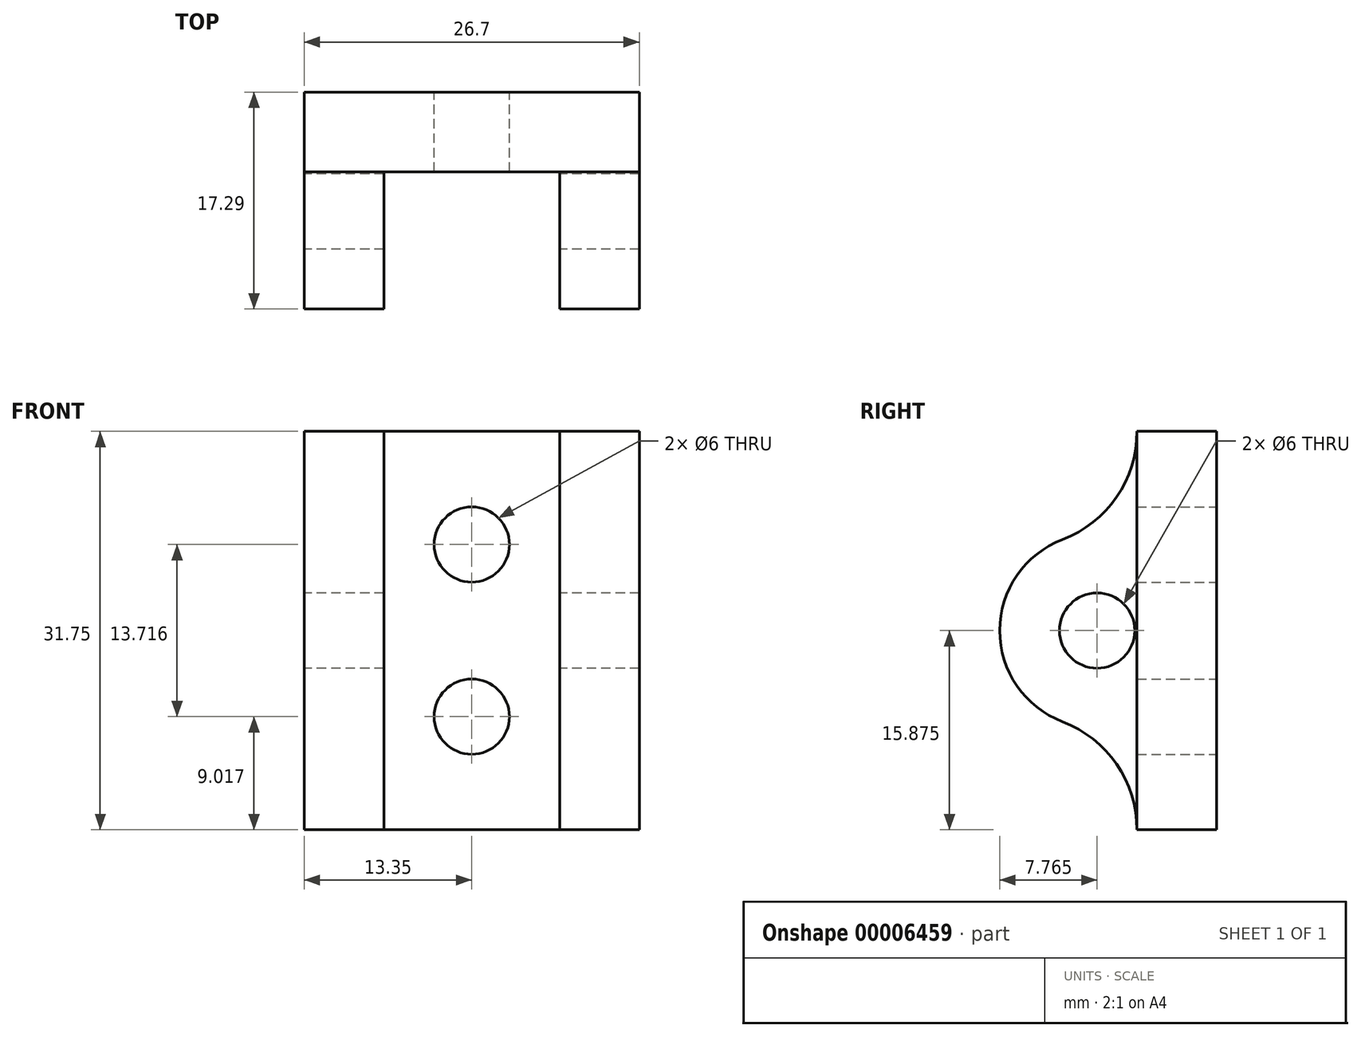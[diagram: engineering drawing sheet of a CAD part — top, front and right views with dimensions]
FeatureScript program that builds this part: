
annotation { "Feature Type Name" : "Feature", "Feature Type Description" : "" }
export const myFeature = defineFeature(function(context is Context, id is Id, definition is map)
    precondition{}
    {
        {
            var Q0;
            Q0=qCreatedBy(makeId("Front.planeOp"),FACE);
            var sketch = newSketch(context, id + "F0", { "sketchPlane" : qUnion([Q0])});
            skLineSegment(sketch, "E0.bottom", {"start": v(0, 0) * mm, "end": v(26.7, 0) * mm});
            skLineSegment(sketch, "E0.top", {"start": v(0, -31.75) * mm, "end": v(26.7, -31.75) * mm});
            skLineSegment(sketch, "E0.left", {"start": v(0, 0) * mm, "end": v(0, -31.75) * mm});
            skLineSegment(sketch, "E0.right", {"start": v(26.7, 0) * mm, "end": v(26.7, -31.75) * mm});
            skCircle(sketch, "E1", {"center": v(13.35, -22.73) * mm, "radius": 3 * mm});
            skCircle(sketch, "E2", {"center": v(13.35, -9.02) * mm, "radius": 3 * mm});
            skLineSegment(sketch, "E3", {"start": v(13.35, -9.02) * mm, "end": v(13.35, -22.73) * mm, "construction": true});
            skPoint(sketch, "E4", {"position": v(13.35, -31.75) * mm});
            skPoint(sketch, "E5", {"position": v(0, -15.88) * mm});
            skPoint(sketch, "E6", {"position": v(13.35, -15.88) * mm});
            skSolve(sketch);
        }
        {
            var Q0;
            Q0 = qSketchRegion(id + "F0", true);
            extrude(context, id + "F1", {"entities" : qUnion([Q0]), "depth" : 6.35 * mm});
        }
        {
            var Q0;
            Q0=makeQuery(id+"F1.opExtrude","SWEPT_FACE",FACE,{"disambiguationData":[OSD([sQuery(id+"F0.wireOp",EDGE,"E0.left")])]});
            var sketch = newSketch(context, id + "F2", { "sketchPlane" : qUnion([Q0])});
            skCircle(sketch, "E7", {"center": v(9.53, -15.88) * mm, "radius": 3 * mm});
            skPoint(sketch, "E8", {"position": v(6.35, -15.88) * mm});
            skArc(sketch, "E9", {"start": v(12.3, -23.13) * mm, "mid": v(17.29, -15.88) * mm, "end": v(12.3, -8.62) * mm});
            skArc(sketch, "E10", {"start": v(12.3, -23.13) * mm, "mid": v(7.98, -26.52) * mm, "end": v(6.35, -31.75) * mm});
            skArc(sketch, "E11", {"start": v(6.35, 0) * mm, "mid": v(7.98, -5.23) * mm, "end": v(12.3, -8.62) * mm});
            skLineSegment(sketch, "E12", {"start": v(6.35, 0) * mm, "end": v(6.35, -31.75) * mm});
            skSolve(sketch);
        }
        {
            var Q0;
            Q0=makeQuery(id+"F2.imprint","IMPRINT",FACE,{"disambiguationData":[TD([[makeQuery(id+"F2.imprint","IMPRINT",EDGE,{"derivedFrom":sQuery(id+"F2.wireOp",EDGE,"E7")}),-1.0]])]});
            var Q1;
            Q1=makeQuery(id+"F1.opExtrude","SWEPT_FACE",FACE,{"disambiguationData":[OSD([sQuery(id+"F0.wireOp",EDGE,"E0.right")])]});
            extrude(context, id + "F3", {"entities" : qUnion([Q0]), "endBound" : BoundingType.UP_TO_SURFACE, "oppositeDirection" : true, "endBoundEntityFace" : qUnion([Q1]), "depth" : 14 * mm + 6.35 * mm});
        }
        {
            var Q0;
            Q0=makeQuery(id+"F3.opExtrude","SWEPT_FACE",FACE,{"disambiguationData":[OSD([sQuery(id+"F2.wireOp",EDGE,"E12")])]});
            var sketch = newSketch(context, id + "F4", { "sketchPlane" : qUnion([Q0])});
            skLineSegment(sketch, "E13.bottom", {"start": v(-20.35, 0) * mm, "end": v(-6.35, 0) * mm});
            skLineSegment(sketch, "E13.top", {"start": v(-20.35, -31.75) * mm, "end": v(-6.35, -31.75) * mm});
            skLineSegment(sketch, "E13.left", {"start": v(-20.35, 0) * mm, "end": v(-20.35, -31.75) * mm});
            skLineSegment(sketch, "E13.right", {"start": v(-6.35, 0) * mm, "end": v(-6.35, -31.75) * mm});
            skLineSegment(sketch, "E14", {"start": v(-26.7, 0) * mm, "end": v(-20.35, 0) * mm, "construction": true});
            skLineSegment(sketch, "E15", {"start": v(-6.35, 0) * mm, "end": v(0, 0) * mm, "construction": true});
            skLineSegment(sketch, "E16", {"start": v(0, 0) * mm, "end": v(-6.35, 0) * mm, "construction": true});
            skSolve(sketch);
        }
        {
            var Q0;
            Q0 = qSketchRegion(id + "F4", true);
            extrude(context, id + "F5", {"entities" : qUnion([Q0]), "operationType" : NewBodyOperationType.REMOVE, "endBound" : BoundingType.THROUGH_ALL, "oppositeDirection" : true, "depth" : 25.4 * mm});
        }
    });
